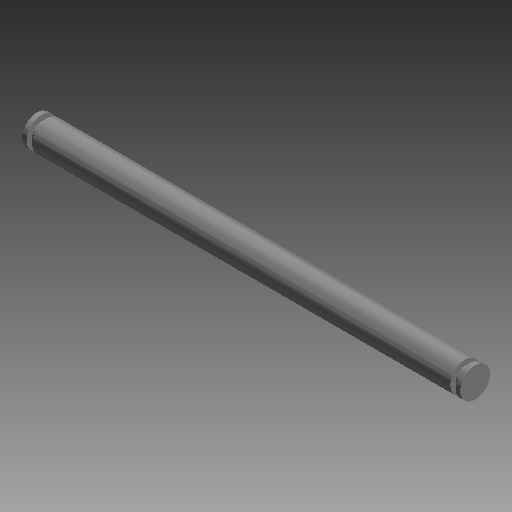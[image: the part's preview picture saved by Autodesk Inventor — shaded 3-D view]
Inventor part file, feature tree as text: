
AUTODESK INVENTOR PART (.ipt)
format: ipt  version: 2019 (Build 230136000, 136)  size: 73,728 bytes
history: native  units: mm (DEFAULTED — no unit token found)
features: revolve x1
ambient origin geometry x8: Origin, YZ Plane, XZ Plane, XY Plane, X Axis, Y Axis, Z Axis, Center Point
bodies: Solid1 (feature_tree)
feature tree (1):
  revolve  "Revolve1"  [1 undecoded]
note: 1 required parameter value undecoded (feature->parameter linkage not recoverable at this tier; creation-order binding heuristic only, values carry confidence <= 0.55)
